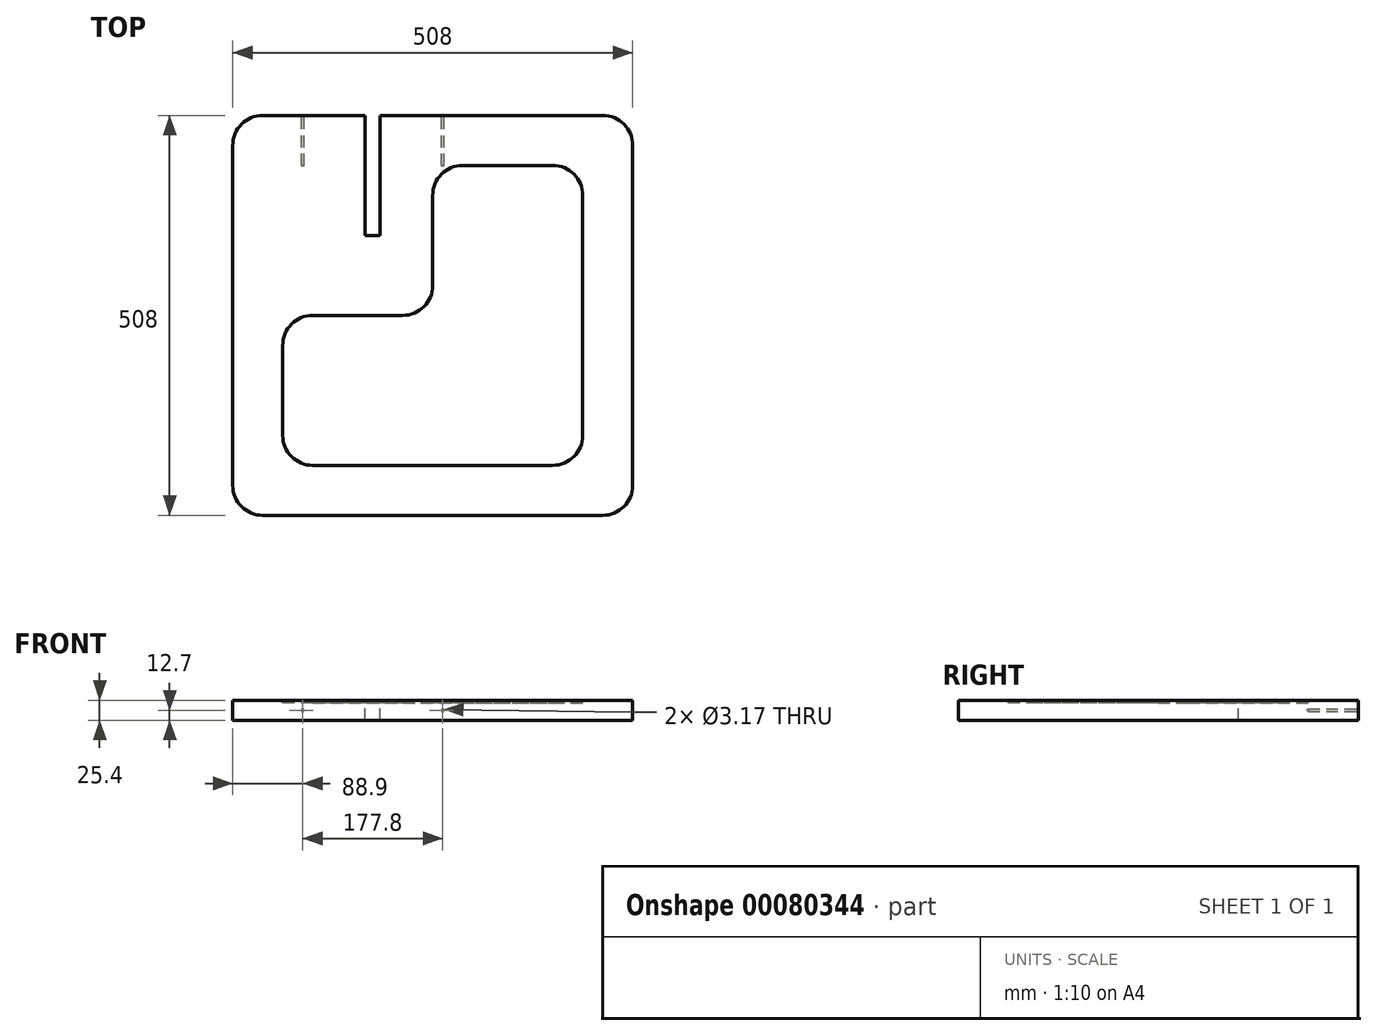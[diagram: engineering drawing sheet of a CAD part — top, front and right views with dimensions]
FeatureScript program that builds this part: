
annotation { "Feature Type Name" : "Feature", "Feature Type Description" : "" }
export const myFeature = defineFeature(function(context is Context, id is Id, definition is map)
    precondition{}
    {
        {
            var Q0;
            Q0=qCreatedBy(makeId("Top.planeOp"),FACE);
            var sketch = newSketch(context, id + "F6", { "sketchPlane" : qUnion([Q0])});
            skLineSegment(sketch, "E0.bottom", {"start": v(254, 254) * mm, "end": v(-254, 254) * mm});
            skLineSegment(sketch, "E0.top", {"start": v(254, -254) * mm, "end": v(-254, -254) * mm});
            skLineSegment(sketch, "E0.left", {"start": v(254, 254) * mm, "end": v(254, -254) * mm});
            skLineSegment(sketch, "E0.right", {"start": v(-254, 254) * mm, "end": v(-254, -254) * mm});
            skPoint(sketch, "E0.middle", {"position": v(0, 0) * mm});
            skSolve(sketch);
        }
        {
            var Q0;
            Q0=makeQuery(id+"F6.imprint","IMPRINT",FACE,{"disambiguationData":[TD([[makeQuery(id+"F6.imprint","IMPRINT",EDGE,{"derivedFrom":sQuery(id+"F6.wireOp",EDGE,"E0.bottom")}),1.0]])]});
            extrude(context, id + "F7", {"entities" : qUnion([Q0]), "depth" : 25.4 * mm});
        }
        {
            var Q0;
            Q0=makeQuery(id+"F7.opExtrude","CAP_FACE",FACE,{"disambiguationData":[OSD([sQuery(id+"F6.wireOp",EDGE,"E0.bottom"),sQuery(id+"F6.wireOp",EDGE,"E0.top"),sQuery(id+"F6.wireOp",EDGE,"E0.left"),sQuery(id+"F6.wireOp",EDGE,"E0.right")])],"isStart":false});
            var sketch = newSketch(context, id + "F8", { "sketchPlane" : qUnion([Q0])});
            skLineSegment(sketch, "E1", {"start": v(0, 0) * mm, "end": v(-254, 0) * mm, "construction": true});
            skLineSegment(sketch, "E2", {"start": v(-254, 0) * mm, "end": v(-254, 254) * mm, "construction": true});
            skLineSegment(sketch, "E3", {"start": v(-254, 254) * mm, "end": v(-85.72, 254) * mm, "construction": true});
            skLineSegment(sketch, "E4", {"start": v(-85.72, 254) * mm, "end": v(-85.72, 101.6) * mm});
            skLineSegment(sketch, "E5", {"start": v(-85.72, 101.6) * mm, "end": v(-66.67, 101.6) * mm});
            skLineSegment(sketch, "E6", {"start": v(-66.67, 101.6) * mm, "end": v(-66.67, 254) * mm});
            skLineSegment(sketch, "E7", {"start": v(-85.72, 254) * mm, "end": v(-66.67, 254) * mm});
            skSolve(sketch);
        }
        {
            var Q0;
            Q0 = qSketchRegion(id + "F8", true);
            extrude(context, id + "F9", {"entities" : qUnion([Q0]), "operationType" : NewBodyOperationType.REMOVE, "oppositeDirection" : true, "depth" : 25.4 * mm});
        }
        {
            var Q0;
            Q0=makeQuery(id+"F7.opExtrude","SWEPT_EDGE",EDGE,{"disambiguationData":[OSD([sQuery(id+"F6.wireOp",EDGE,"E0.top"),sQuery(id+"F6.wireOp",EDGE,"E0.left")])]});
            var Q1;
            Q1=makeQuery(id+"F7.opExtrude","SWEPT_EDGE",EDGE,{"disambiguationData":[OSD([sQuery(id+"F6.wireOp",EDGE,"E0.bottom"),sQuery(id+"F6.wireOp",EDGE,"E0.left")])]});
            var Q2;
            Q2=makeQuery(id+"F7.opExtrude","SWEPT_EDGE",EDGE,{"disambiguationData":[OSD([sQuery(id+"F6.wireOp",EDGE,"E0.bottom"),sQuery(id+"F6.wireOp",EDGE,"E0.right")])]});
            var Q3;
            Q3=makeQuery(id+"F7.opExtrude","SWEPT_EDGE",EDGE,{"disambiguationData":[OSD([sQuery(id+"F6.wireOp",EDGE,"E0.top"),sQuery(id+"F6.wireOp",EDGE,"E0.right")])]});
            fillet(context, id + "F0", {"entities" : qUnion([Q0, Q1, Q2, Q3]), "radius" : 38.1 * mm, "tangentPropagation" : true, "allowEdgeOverflow" : false});
        }
        {
            var Q0;
            Q0=makeQuery(id+"F7.opExtrude","CAP_FACE",FACE,{"disambiguationData":[OSD([sQuery(id+"F6.wireOp",EDGE,"E0.bottom"),sQuery(id+"F6.wireOp",EDGE,"E0.top"),sQuery(id+"F6.wireOp",EDGE,"E0.left"),sQuery(id+"F6.wireOp",EDGE,"E0.right")])],"isStart":false});
            var sketch = newSketch(context, id + "F1", { "sketchPlane" : qUnion([Q0])});
            skLineSegment(sketch, "E8.top", {"start": v(0, 190.5) * mm, "end": v(190.5, 190.5) * mm});
            skLineSegment(sketch, "E8.left", {"start": v(0, 0) * mm, "end": v(0, 190.5) * mm});
            skLineSegment(sketch, "E9.bottom", {"start": v(0, 0) * mm, "end": v(-190.5, 0) * mm});
            skLineSegment(sketch, "E9.right", {"start": v(-190.5, 0) * mm, "end": v(-190.5, -190.5) * mm});
            skLineSegment(sketch, "E10", {"start": v(190.5, 190.5) * mm, "end": v(190.5, -190.5) * mm});
            skLineSegment(sketch, "E11", {"start": v(-190.5, -190.5) * mm, "end": v(190.5, -190.5) * mm});
            skSolve(sketch);
        }
        {
            var Q0;
            Q0 = qSketchRegion(id + "F1", true);
            extrude(context, id + "F2", {"entities" : qUnion([Q0]), "operationType" : NewBodyOperationType.REMOVE, "oppositeDirection" : true, "depth" : 3.17 * mm});
        }
        {
            var Q0;
            Q0=makeQuery(id+"F2.boolean.opBoolean","COPY",EDGE,{"derivedFrom":makeQuery(id+"F2.opExtrude","SWEPT_EDGE",EDGE,{"disambiguationData":[OSD([sQuery(id+"F1.wireOp",EDGE,"E8.left"),sQuery(id+"F1.wireOp",EDGE,"E9.bottom")])]})});
            var Q1;
            Q1=makeQuery(id+"F2.boolean.opBoolean","COPY",EDGE,{"derivedFrom":makeQuery(id+"F2.opExtrude","SWEPT_EDGE",EDGE,{"disambiguationData":[OSD([sQuery(id+"F1.wireOp",EDGE,"E8.top"),sQuery(id+"F1.wireOp",EDGE,"E8.left")])]})});
            var Q2;
            Q2=makeQuery(id+"F2.boolean.opBoolean","COPY",EDGE,{"derivedFrom":makeQuery(id+"F2.opExtrude","SWEPT_EDGE",EDGE,{"disambiguationData":[OSD([sQuery(id+"F1.wireOp",EDGE,"E8.top"),sQuery(id+"F1.wireOp",EDGE,"E10")])]})});
            var Q3;
            Q3=makeQuery(id+"F2.boolean.opBoolean","COPY",EDGE,{"derivedFrom":makeQuery(id+"F2.opExtrude","SWEPT_EDGE",EDGE,{"disambiguationData":[OSD([sQuery(id+"F1.wireOp",EDGE,"E9.right"),sQuery(id+"F1.wireOp",EDGE,"E11")])]})});
            var Q4;
            Q4=makeQuery(id+"F2.boolean.opBoolean","COPY",EDGE,{"derivedFrom":makeQuery(id+"F2.opExtrude","SWEPT_EDGE",EDGE,{"disambiguationData":[OSD([sQuery(id+"F1.wireOp",EDGE,"E10"),sQuery(id+"F1.wireOp",EDGE,"E11")])]})});
            var Q5;
            Q5=makeQuery(id+"F2.boolean.opBoolean","COPY",EDGE,{"derivedFrom":makeQuery(id+"F2.opExtrude","SWEPT_EDGE",EDGE,{"disambiguationData":[OSD([sQuery(id+"F1.wireOp",EDGE,"E9.bottom"),sQuery(id+"F1.wireOp",EDGE,"E9.right")])]})});
            fillet(context, id + "F3", {"entities" : qUnion([Q0, Q1, Q2, Q3, Q4, Q5]), "radius" : 38.1 * mm, "tangentPropagation" : true, "allowEdgeOverflow" : false});
        }
        {
            var Q0;
            {var subQ1=sQuery(id+"F6.wireOp",EDGE,"E0.left");var subQ3=sQuery(id+"F6.wireOp",EDGE,"E0.bottom");Q0=makeQuery(id+"F9.boolean.opBoolean","SPLIT",FACE,{"disambiguationData":[TD([makeQuery(id+"F7.opExtrude","SWEPT_FACE",FACE,{"disambiguationData":[OSD([subQ1])]})])],"derivedFrom":makeQuery(id+"F7.opExtrude","SWEPT_FACE",FACE,{"disambiguationData":[OSD([subQ3])]})});}
            var sketch = newSketch(context, id + "F4", { "sketchPlane" : qUnion([Q0])});
            skPoint(sketch, "E12", {"position": v(-12.7, 12.7) * mm});
            skPoint(sketch, "E13", {"position": v(165.1, 12.7) * mm});
            skSolve(sketch);
        }
        {
            var Q0;
            Q0=sQuery(id+"F4.wireOp",VERTEX,"E12");
            var Q1;
            Q1=sQuery(id+"F4.wireOp",VERTEX,"E13");
            var Q2;
            Q2=makeQuery(id+"F7.opExtrude","SWEPT_BODY",BODY,{"disambiguationData":[OSD([sQuery(id+"F6.wireOp",EDGE,"E0.bottom"),sQuery(id+"F6.wireOp",EDGE,"E0.top"),sQuery(id+"F6.wireOp",EDGE,"E0.left"),sQuery(id+"F6.wireOp",EDGE,"E0.right")])]});
            hole(context, id + "F5", {"style" : HoleStyle.SIMPLE, "endStyle" : HoleEndStyle.BLIND, "holeDiameter" : 3.17 * mm, "holeDepth" : 63.5 * mm, "locations" : qUnion([Q0, Q1]), "scope" : qUnion([Q2])});
        }
    });
